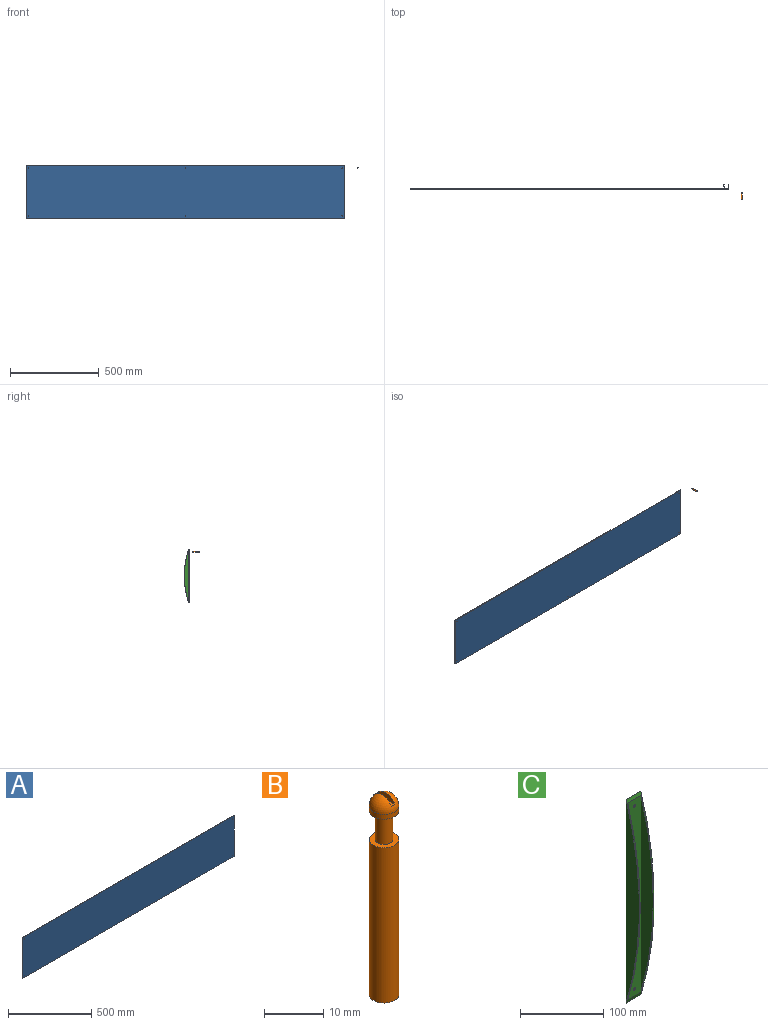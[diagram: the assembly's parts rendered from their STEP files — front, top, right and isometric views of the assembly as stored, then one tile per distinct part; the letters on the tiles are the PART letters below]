
ASSEMBLY  parts=3 mates=1
PART A: 12 faces, bbox 1800x4.5x300 mm
  f0: plane 1800x4.5mm, normal (0,0,1), area 8100mm2, adj f1,f9,f10,f11
  f1: plane 300x4.5mm, normal (-1,0,0), area 1350mm2, adj f0,f2,f10,f11
  f2: plane 1800x4.5mm, normal (0,0,-1), area 8100mm2, adj f1,f9,f10,f11
  f3: cylinder r=1.5mm len=4.5mm, axis (0,1,0), area 42.4mm2, adj f10,f11
  f4: cylinder r=1.5mm len=4.5mm, axis (0,1,0), area 42.4mm2, adj f10,f11
  f5: cylinder r=1.5mm len=4.5mm, axis (0,1,0), area 42.4mm2, adj f10,f11
  f6: cylinder r=1.5mm len=4.5mm, axis (0,1,0), area 42.4mm2, adj f10,f11
  f7: cylinder r=1.5mm len=4.5mm, axis (0,1,0), area 42.4mm2, adj f10,f11
  f8: cylinder r=1.5mm len=4.5mm, axis (0,1,0), area 42.4mm2, adj f10,f11
  f9: plane 300x4.5mm, normal (1,0,0), area 1350mm2, adj f0,f2,f10,f11
  f10: plane 1800x300mm, normal (0,-1,0), area 539957.6mm2, adj f0,f1,f2,f3,f4,f5,f6,f7
  f11: plane 1800x300mm, normal (0,1,0), area 539957.6mm2, adj f0,f1,f2,f3,f4,f5,f6,f7
PART B: 10 faces, bbox 5x5x41.5 mm
  f0: plane 5x5mm, normal (0,0,1), area 12.6mm2, adj f1,f6
  f1: cylinder r=2.5mm len=32.08mm, axis (0,0,1), area 503.8mm2, adj f0,f2
  f2: plane 5x5mm, normal (0,0,-1), area 19.6mm2, adj f1
  f3: sphere r=2.5mm, area 34.9mm2, adj f4,f7,f8,f9
  f4: cylinder r=2.5mm len=5mm, axis (0,0,1), area 15.7mm2, adj f3,f5
  f5: plane 5x5mm, normal (0,0,-1), area 12.6mm2, adj f4,f6
  f6: cylinder r=1.5mm len=5.93mm, axis (0,0,1), area 55.9mm2, adj f0,f5
  f7: plane 4.32x1.28mm, normal (1,0,0), area 3.9mm2, adj f3,f8
  f8: plane 4.4x0.82mm, normal (0,0,1), area 3.6mm2, adj f3,f7,f9
  f9: plane 4.32x1.28mm, normal (-1,0,0), area 3.9mm2, adj f3,f8
PART C: 9 faces, bbox 25.4x22.6x300 mm
  f0: plane 289.51x22.23mm, normal (0,-1,0), area 6415.2mm2, adj f1,f2,f3,f7,f8
  f1: plane 289.51x21.04mm, normal (-1,0,0), area 4077.3mm2, adj f0,f3
  f2: plane 289.51x21.04mm, normal (1,0,0), area 4077.3mm2, adj f0,f3
  f3: cylinder r=508.57mm len=300mm, axis (1,0,0), area 1210.4mm2, adj f0,f1,f2,f4,f5,f6
  f4: plane 300x22.62mm, normal (1,0,0), area 4545.3mm2, adj f3,f6
  f5: plane 300x22.62mm, normal (-1,0,0), area 4545.3mm2, adj f3,f6
  f6: plane 300x25.4mm, normal (0,1,0), area 7600.8mm2, adj f3,f4,f5,f7,f8
  f7: cylinder r=1.75mm len=3.5mm, axis (0,1,0), area 17.5mm2, adj f0,f6
  f8: cylinder r=1.75mm len=3.5mm, axis (0,1,0), area 17.5mm2, adj f0,f6
PLACE A t=(-1469.66,80.25,275.94)mm
PLACE B rot(axis=(-1,0,0),90deg) t=(401.81,55.98,562.1)mm
PLACE C rot(axis=(1,0,0),180deg) t=(302.64,105.65,575.94)mm
MATE cylindrical A.f5 <-> C.f7  axis (0,1,0) through (315.34,80.25,560.94)mm
